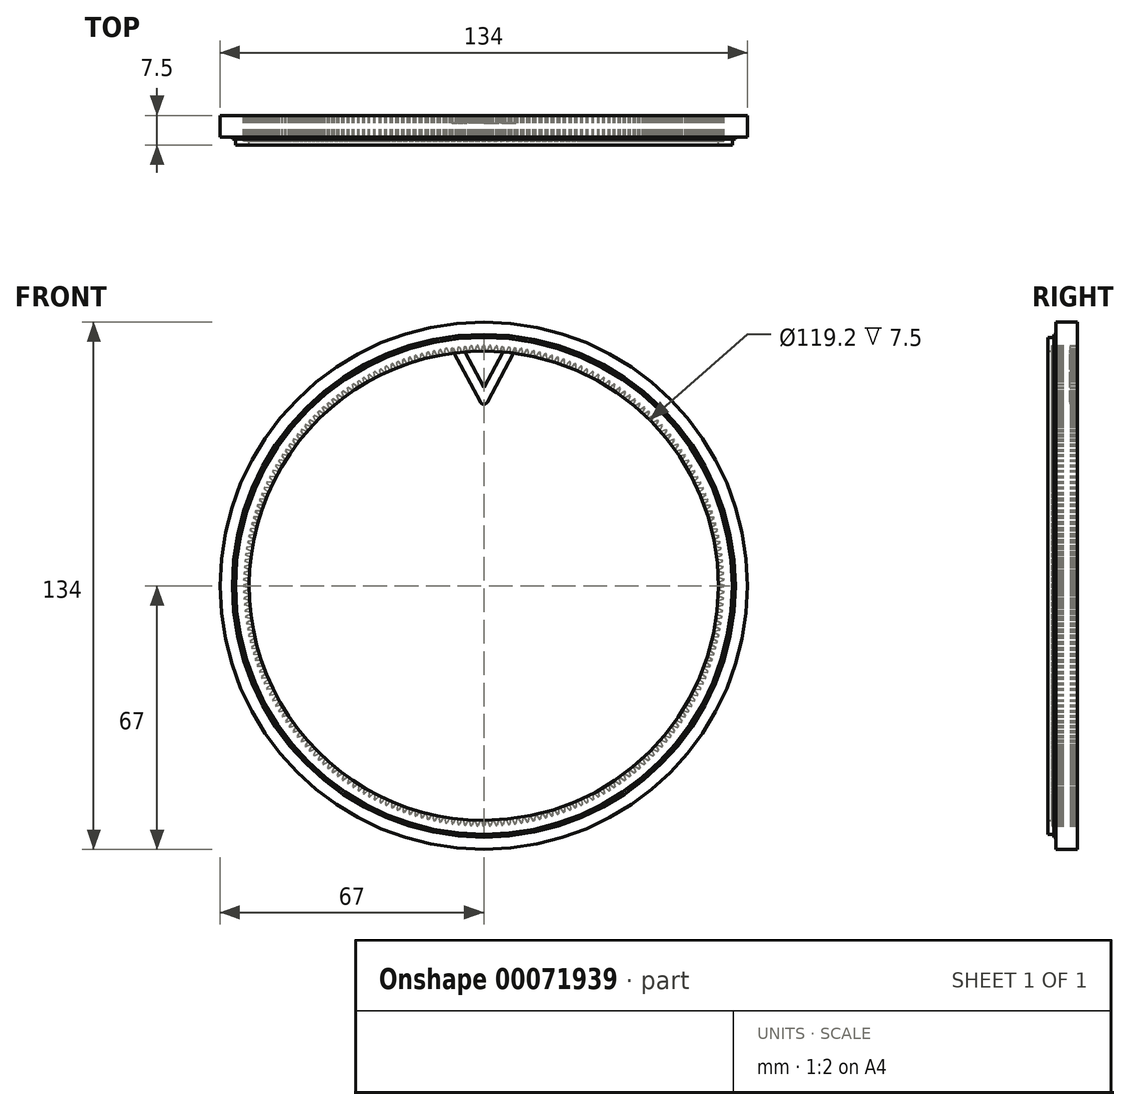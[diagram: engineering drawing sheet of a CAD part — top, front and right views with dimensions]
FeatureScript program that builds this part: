
annotation { "Feature Type Name" : "Feature", "Feature Type Description" : "" }
export const myFeature = defineFeature(function(context is Context, id is Id, definition is map)
    precondition{}
    {
        {
            var Q0;
            Q0=qCreatedBy(makeId("Front.planeOp"),FACE);
            var sketch = newSketch(context, id + "F0", { "sketchPlane" : qUnion([Q0])});
            skCircle(sketch, "E0", {"center": v(0, 0) * mm, "radius": 67 * mm});
            skCircle(sketch, "E1", {"center": v(0, 0) * mm, "radius": 59.6 * mm});
            skSolve(sketch);
        }
        {
            var Q0;
            Q0=makeQuery(id+"F0.imprint","IMPRINT",FACE,{"disambiguationData":[TD([[makeQuery(id+"F0.imprint","IMPRINT",EDGE,{"derivedFrom":sQuery(id+"F0.wireOp",EDGE,"E0")}),1.0]])]});
            extrude(context, id + "F1", {"entities" : qUnion([Q0]), "endBound" : BoundingType.SYMMETRIC, "depth" : 7.5 * mm});
        }
        {
            var Q0;
            Q0=makeQuery(id+"F1.opExtrude","CAP_FACE",FACE,{"disambiguationData":[OSD([sQuery(id+"F0.wireOp",EDGE,"E0"),sQuery(id+"F0.wireOp",EDGE,"E1")])],"isStart":false});
            var sketch = newSketch(context, id + "F2", { "sketchPlane" : qUnion([Q0])});
            skCircle(sketch, "E2", {"center": v(0, 0) * mm, "radius": 63.12 * mm});
            skCircle(sketch, "E3", {"center": v(0, 0) * mm, "radius": 63.88 * mm});
            skSolve(sketch);
        }
        {
            var Q0;
            Q0=makeQuery(id+"F2.imprint","IMPRINT",FACE,{"disambiguationData":[TD([[makeQuery(id+"F2.imprint","IMPRINT",EDGE,{"derivedFrom":sQuery(id+"F2.wireOp",EDGE,"E2")}),-1.0]])]});
            extrude(context, id + "F3", {"entities" : qUnion([Q0]), "operationType" : NewBodyOperationType.REMOVE, "oppositeDirection" : true, "depth" : 1.5 * mm});
        }
        {
            var Q0;
            {var subQ0=sQuery(id+"F0.wireOp",EDGE,"E0");Q0=makeQuery(id+"F3.boolean.opBoolean","SPLIT",FACE,{"disambiguationData":[TD([makeQuery(id+"F1.opExtrude","SWEPT_FACE",FACE,{"disambiguationData":[OSD([subQ0])]})])],"derivedFrom":makeQuery(id+"F1.opExtrude","CAP_FACE",FACE,{"disambiguationData":[OSD([subQ0,sQuery(id+"F0.wireOp",EDGE,"E1")])],"isStart":false})});}
            extrude(context, id + "F4", {"entities" : qUnion([Q0]), "operationType" : NewBodyOperationType.REMOVE, "oppositeDirection" : true, "depth" : 2 * mm});
        }
        {
            var Q0;
            Q0=makeQuery(id+"F1.opExtrude","CAP_FACE",FACE,{"disambiguationData":[OSD([sQuery(id+"F0.wireOp",EDGE,"E0"),sQuery(id+"F0.wireOp",EDGE,"E1")])],"isStart":true});
            var sketch = newSketch(context, id + "F5", { "sketchPlane" : qUnion([Q0])});
            skCircle(sketch, "E4", {"center": v(0, 0) * mm, "radius": 61 * mm, "construction": true});
            skLineSegment(sketch, "E5", {"start": v(0, 0) * mm, "end": v(61, 0) * mm, "construction": true});
            skLineSegment(sketch, "E6", {"start": v(61, 0.15) * mm, "end": v(61, -0.15) * mm});
            skLineSegment(sketch, "E7", {"start": v(59.4, 0.67) * mm, "end": v(59.4, -0.67) * mm});
            skPoint(sketch, "E8", {"position": v(59.4, 0) * mm});
            skLineSegment(sketch, "E9", {"start": v(59.4, 0.68) * mm, "end": v(61, 0.15) * mm});
            skLineSegment(sketch, "E10", {"start": v(59.4, -0.68) * mm, "end": v(61, -0.15) * mm});
            skSolve(sketch);
        }
        {
            var Q0;
            {var subQ0=sQuery(id+"F5.wireOp",EDGE,"E7");Q0=makeQuery(id+"F5.imprint","IMPRINT",FACE,{"disambiguationData":[TD([[makeQuery(id+"F5.imprint","IMPRINT",EDGE,{"derivedFrom":subQ0}),1.0]])]});}
            var Q1;
            {var subQ0=sQuery(id+"F5.wireOp",EDGE,"E6");Q1=makeQuery(id+"F5.imprint","IMPRINT",FACE,{"disambiguationData":[TD([[makeQuery(id+"F5.imprint","IMPRINT",EDGE,{"derivedFrom":subQ0}),-1.0]])]});}
            extrude(context, id + "F6", {"entities" : qUnion([Q0, Q1]), "operationType" : NewBodyOperationType.REMOVE, "oppositeDirection" : true, "depth" : 6.5 * mm});
        }
        {
            var Q0;
            Q0=makeQuery(id+"F6.boolean.opBoolean","COPY",FACE,{"derivedFrom":makeQuery(id+"F6.opExtrude","SWEPT_FACE",FACE,{"disambiguationData":[OSD([sQuery(id+"F5.wireOp",EDGE,"E9")])]})});
            var Q1;
            Q1=makeQuery(id+"F6.boolean.opBoolean","COPY",FACE,{"derivedFrom":makeQuery(id+"F6.opExtrude","CAP_FACE",FACE,{"disambiguationData":[OSD([sQuery(id+"F5.wireOp",EDGE,"E6"),sQuery(id+"F5.wireOp",EDGE,"E7"),sQuery(id+"F5.wireOp",EDGE,"E9"),sQuery(id+"F5.wireOp",EDGE,"E10")])],"isStart":false})});
            var Q2;
            Q2=makeQuery(id+"F6.boolean.opBoolean","COPY",FACE,{"derivedFrom":makeQuery(id+"F6.opExtrude","SWEPT_FACE",FACE,{"disambiguationData":[OSD([sQuery(id+"F5.wireOp",EDGE,"E6")])]})});
            var Q3;
            Q3=makeQuery(id+"F6.boolean.opBoolean","COPY",FACE,{"derivedFrom":makeQuery(id+"F6.opExtrude","SWEPT_FACE",FACE,{"disambiguationData":[OSD([sQuery(id+"F5.wireOp",EDGE,"E10")])]})});
            var Q4;
            Q4=sQuery(id+"F5.wireOp",EDGE,"E4");
            circularPattern(context, id + "F7", {"faces" : qUnion([Q0, Q1, Q2, Q3]), "axis" : qUnion([Q4]), "angle" : 360 * degree, "instanceCount" : 240, "equalSpace" : true, "patternType" : PatternType.FACE});
        }
        {
            var Q0;
            Q0=makeQuery(id+"F1.opExtrude","CAP_FACE",FACE,{"disambiguationData":[OSD([sQuery(id+"F0.wireOp",EDGE,"E0"),sQuery(id+"F0.wireOp",EDGE,"E1")])],"isStart":true});
            var sketch = newSketch(context, id + "F8", { "sketchPlane" : qUnion([Q0])});
            skLineSegment(sketch, "E11", {"start": v(0, 45) * mm, "end": v(0, 72.03) * mm, "construction": true});
            skCircle(sketch, "E12", {"center": v(0, 0) * mm, "radius": 63 * mm, "construction": true});
            skLineSegment(sketch, "E13", {"start": v(0, 45) * mm, "end": v(14.66, 72.57) * mm, "construction": true});
            skLineSegment(sketch, "E14", {"start": v(0, 45) * mm, "end": v(9.21, 62.32) * mm});
            skLineSegment(sketch, "E15", {"start": v(9.21, 62.32) * mm, "end": v(0, 62.32) * mm});
            skLineSegment(sketch, "E16.MirrorCS", {"start": v(-9.21, 62.32) * mm, "end": v(0, 62.32) * mm});
            skLineSegment(sketch, "E17.MirrorCS", {"start": v(0, 45) * mm, "end": v(-9.21, 62.32) * mm});
            skLineSegment(sketch, "E18.0", {"start": v(5.05, 59.82) * mm, "end": v(0, 59.82) * mm});
            skLineSegment(sketch, "E18.1", {"start": v(0, 50.33) * mm, "end": v(5.05, 59.82) * mm});
            skLineSegment(sketch, "E18.2", {"start": v(0, 50.33) * mm, "end": v(-5.05, 59.82) * mm});
            skLineSegment(sketch, "E18.3", {"start": v(-5.05, 59.82) * mm, "end": v(0, 59.82) * mm});
            skSolve(sketch);
        }
        {
            var Q0;
            {var subQ17=sQuery(id+"F8.wireOp",EDGE,"E18.1");Q0=makeQuery(id+"F8.imprint","IMPRINT",FACE,{"disambiguationData":[TD([[makeQuery(id+"F8.imprint","IMPRINT",EDGE,{"derivedFrom":subQ17}),-1.0]])]});}
            var Q1;
            {var subQ42=sQuery(id+"F8.wireOp",EDGE,"E15");Q1=makeQuery(id+"F8.imprint","IMPRINT",FACE,{"disambiguationData":[TD([[makeQuery(id+"F8.imprint","IMPRINT",EDGE,{"derivedFrom":subQ42}),1.0]])]});}
            extrude(context, id + "F9", {"entities" : qUnion([Q0, Q1]), "operationType" : NewBodyOperationType.ADD, "oppositeDirection" : true, "depth" : 2 * mm});
        }
        {
            var Q0;
            Q0=makeQuery(id+"F9.opExtrude","SWEPT_EDGE",EDGE,{"disambiguationData":[OSD([sQuery(id+"F8.wireOp",EDGE,"E14"),sQuery(id+"F8.wireOp",EDGE,"E17.MirrorCS")])]});
            fillet(context, id + "F10", {"entities" : qUnion([Q0]), "radius" : 1 * mm, "tangentPropagation" : true, "allowEdgeOverflow" : false});
        }
    });
